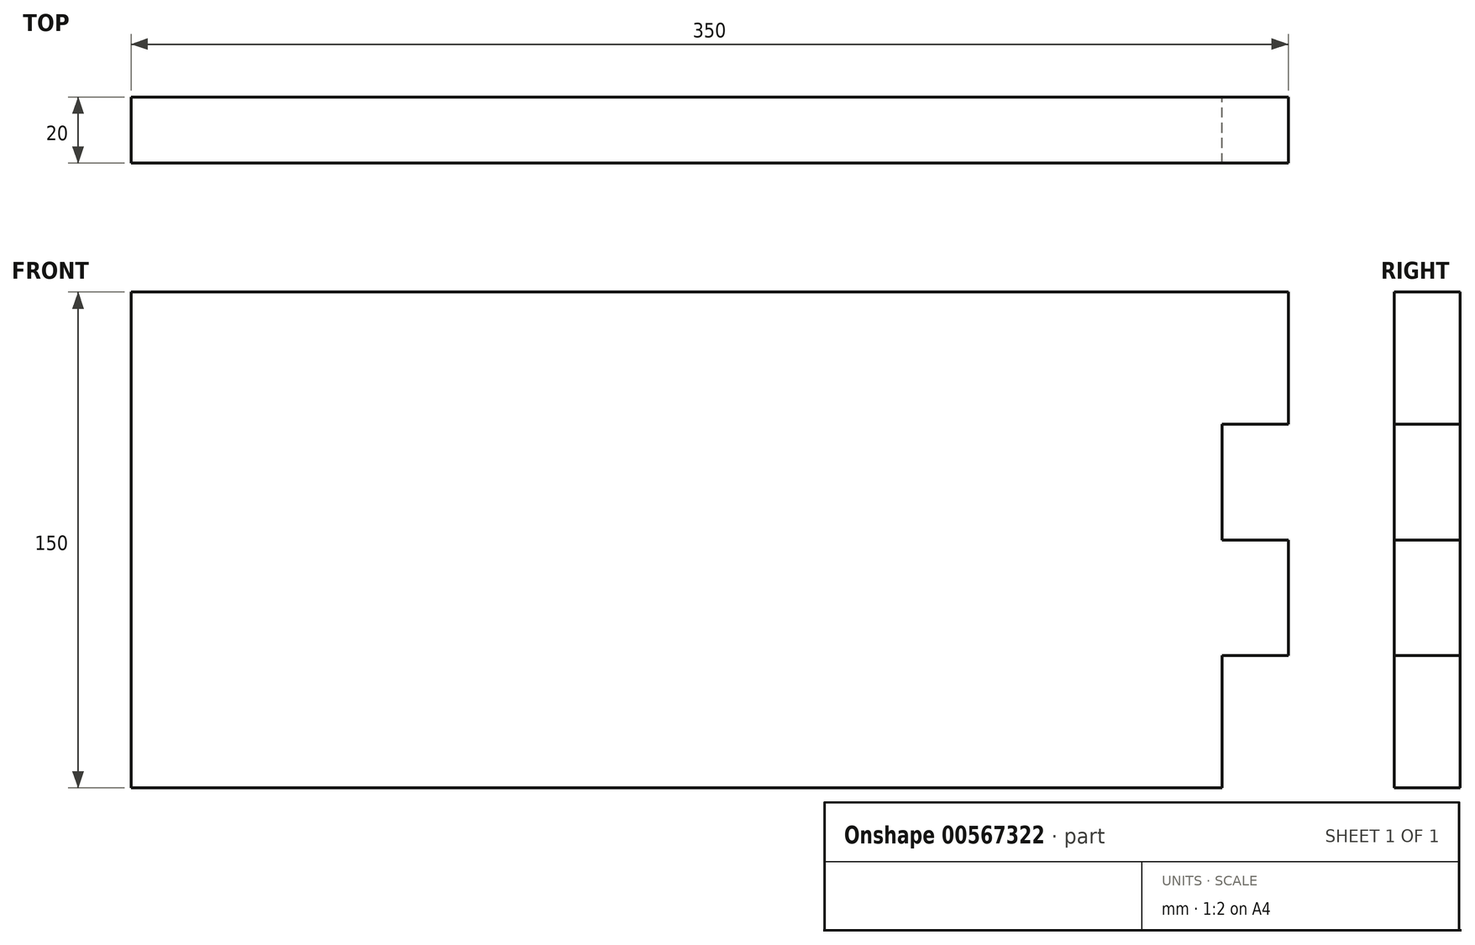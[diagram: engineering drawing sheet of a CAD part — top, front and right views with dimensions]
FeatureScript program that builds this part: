
annotation { "Feature Type Name" : "Feature", "Feature Type Description" : "" }
export const myFeature = defineFeature(function(context is Context, id is Id, definition is map)
    precondition{}
    {
        {
            var Q0;
            Q0=qCreatedBy(makeId("Front.planeOp"),FACE);
            var sketch = newSketch(context, id + "F0", { "sketchPlane" : qUnion([Q0])});
            skLineSegment(sketch, "E0.bottom", {"start": v(-183.5, 40) * mm, "end": v(166.5, 40) * mm});
            skLineSegment(sketch, "E0.top", {"start": v(-183.5, -110) * mm, "end": v(146.5, -110) * mm});
            skLineSegment(sketch, "E0.left", {"start": v(-183.5, 40) * mm, "end": v(-183.5, -110) * mm});
            skLineSegment(sketch, "E0.right", {"start": v(166.5, 40) * mm, "end": v(166.5, 0) * mm});
            skLineSegment(sketch, "E1", {"start": v(146.5, 40) * mm, "end": v(146.5, -110) * mm});
            skLineSegment(sketch, "E2", {"start": v(146.5, -35) * mm, "end": v(166.5, -35) * mm});
            skLineSegment(sketch, "E3", {"start": v(146.5, 0) * mm, "end": v(166.5, 0) * mm});
            skLineSegment(sketch, "E4", {"start": v(146.5, -70) * mm, "end": v(166.5, -70) * mm});
            skLineSegment(sketch, "E5.trimOffspring", {"start": v(166.5, -35) * mm, "end": v(166.5, -70) * mm});
            skPoint(sketch, "E6.orphan", {"position": v(166.5, -110) * mm});
            skSolve(sketch);
        }
        {
            var Q0;
            Q0 = qSketchRegion(id + "F0", true);
            extrude(context, id + "F1", {"entities" : qUnion([Q0]), "depth" : 20 * mm, "offsetDistance" : 25.4 * mm});
        }
    });
